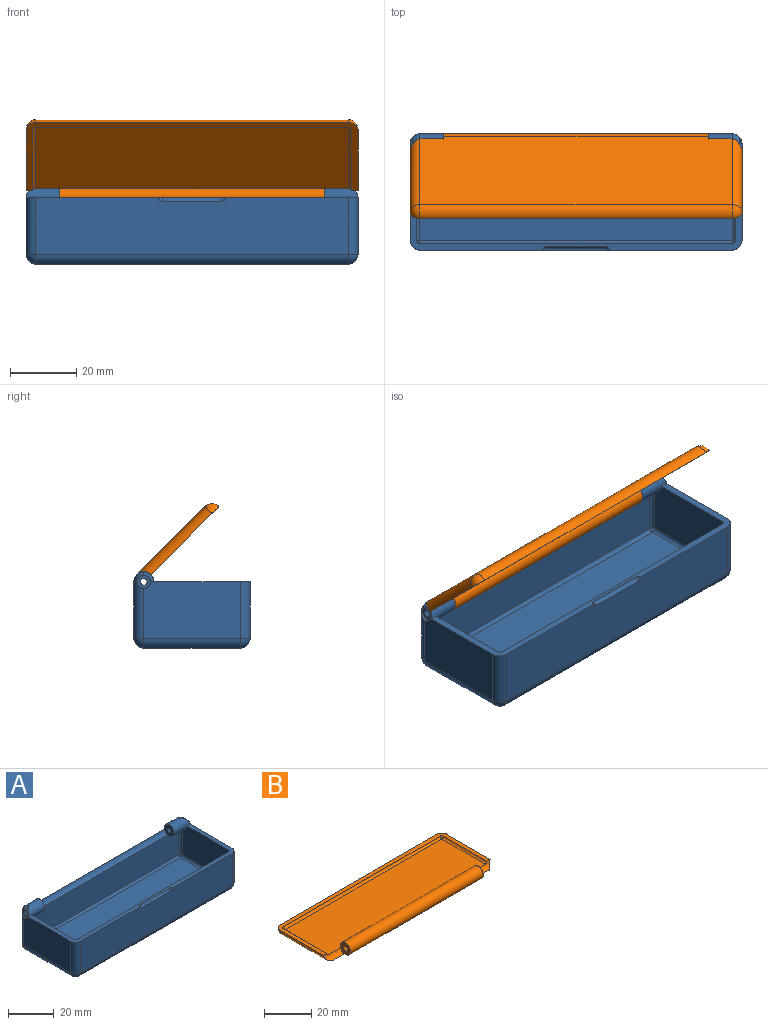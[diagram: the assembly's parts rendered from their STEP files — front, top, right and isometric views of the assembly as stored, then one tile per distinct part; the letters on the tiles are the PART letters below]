
ASSEMBLY  parts=2 mates=1
PART A: 53 faces, bbox 100x35x23 mm
  f0: plane 94x17mm, normal (0,-1,0), area 1578.4mm2, adj f1,f12,f13,f19,f50,f51,f52
  f1: plane 100x29mm, normal (0,0,1), area 285mm2, adj f0,f6,f9,f11,f12,f13,f23,f29
  f2: cylinder r=3mm len=17mm, axis (0,0,-1), area 76.8mm2, adj f5,f9,f10,f16,f24
  f3: cylinder r=3mm len=17mm, axis (0,0,-1), area 76.8mm2, adj f7,f10,f11,f20,f25
  f4: cylinder r=3mm len=3mm, axis (0,-1,0), area 5.6mm2, adj f5,f6,f9,f24
  f5: sphere r=3mm, area 10.5mm2, adj f2,f4,f6,f24
  f6: cylinder r=3mm len=10mm, axis (1,0,0), area 120.6mm2, adj f1,f4,f5,f10,f28,f29,f30,f47
  f7: sphere r=3mm, area 10.5mm2, adj f3,f8,f23,f25
  f8: cylinder r=3mm len=3mm, axis (0,1,0), area 5.6mm2, adj f7,f11,f23,f25
  f9: plane 29x17mm, normal (1,0,0), area 489.9mm2, adj f1,f2,f4,f13,f15,f24
  f10: plane 94x17mm, normal (0,1,0), area 1535.5mm2, adj f2,f3,f6,f18,f23,f45,f46,f47
  f11: plane 29x17mm, normal (-1,0,0), area 489.9mm2, adj f1,f3,f8,f12,f22,f25
  f12: cylinder r=3mm len=17mm, axis (0,0,-1), area 80.1mm2, adj f0,f1,f11,f21
  f13: cylinder r=3mm len=17mm, axis (0,0,-1), area 80.1mm2, adj f0,f1,f9,f17
  f14: plane 94x29mm, normal (0,0,-1), area 2726mm2, adj f15,f18,f19,f22
  f15: cylinder r=3mm len=29mm, axis (0,1,0), area 136.7mm2, adj f9,f14,f16,f17
  f16: sphere r=3mm, area 14.1mm2, adj f2,f15,f18
  f17: sphere r=3mm, area 14.1mm2, adj f13,f15,f19
  f18: cylinder r=3mm len=94mm, axis (-1,0,0), area 443mm2, adj f10,f14,f16,f20
  f19: cylinder r=3mm len=94mm, axis (1,0,0), area 443mm2, adj f0,f14,f17,f21
  f20: sphere r=3mm, area 14.1mm2, adj f3,f18,f22
  f21: sphere r=3mm, area 14.1mm2, adj f12,f19,f22
  f22: cylinder r=3mm len=29mm, axis (0,-1,0), area 136.7mm2, adj f11,f14,f20,f21
  f23: cylinder r=3mm len=10mm, axis (1,0,0), area 120.6mm2, adj f1,f7,f8,f10,f28,f31,f32,f46
  f24: cylinder r=2mm len=4mm, axis (1,0,0), area 7.9mm2, adj f2,f4,f5,f9,f48
  f25: cylinder r=2mm len=4mm, axis (1,0,0), area 7.9mm2, adj f3,f7,f8,f11,f49
  f26: cylinder r=1mm len=9mm, axis (1,0,0), area 56.5mm2, adj f46,f49
  f27: cylinder r=1mm len=9mm, axis (1,0,0), area 56.5mm2, adj f47,f48
  f28: plane 94x14.17mm, normal (0,-1,0), area 1323.7mm2, adj f6,f23,f30,f31,f44,f45,f46,f47
  f29: plane 29x17mm, normal (-1,0,0), area 485.9mm2, adj f1,f6,f30,f35,f41
  f30: cylinder r=1mm len=14.17mm, axis (0,0,-1), area 22.1mm2, adj f6,f28,f29,f43
  f31: cylinder r=1mm len=14.17mm, axis (0,0,-1), area 22.1mm2, adj f23,f28,f32,f42
  f32: plane 29x17mm, normal (1,0,0), area 485.9mm2, adj f1,f23,f31,f33,f40
  f33: cylinder r=1mm len=17mm, axis (0,0,-1), area 26.7mm2, adj f1,f32,f34,f38
  f34: plane 94x17mm, normal (0,1,0), area 1598mm2, adj f1,f33,f35,f37
  f35: cylinder r=1mm len=17mm, axis (0,0,-1), area 26.7mm2, adj f1,f29,f34,f39
  f36: plane 94x29mm, normal (0,0,1), area 2726mm2, adj f37,f40,f41,f44
  f37: cylinder r=1mm len=94mm, axis (1,0,0), area 147.7mm2, adj f34,f36,f38,f39
  f38: sphere r=1mm, area 1.6mm2, adj f33,f37,f40
  f39: sphere r=1mm, area 1.6mm2, adj f35,f37,f41
  f40: cylinder r=1mm len=29mm, axis (0,-1,0), area 45.6mm2, adj f32,f36,f38,f42
  f41: cylinder r=1mm len=29mm, axis (0,1,0), area 45.6mm2, adj f29,f36,f39,f43
  f42: sphere r=1mm, area 1.6mm2, adj f31,f40,f44
  f43: sphere r=1mm, area 1.6mm2, adj f30,f41,f44
  f44: cylinder r=1mm len=94mm, axis (-1,0,0), area 147.7mm2, adj f28,f36,f42,f43
  f45: cylinder r=3.1mm len=80mm, axis (1,0,0), area 244.9mm2, adj f10,f28,f46,f47
  f46: plane 6x6mm, normal (1,0,0), area 25.5mm2, adj f10,f23,f26,f28,f45
  f47: plane 6x6mm, normal (-1,0,0), area 25.5mm2, adj f6,f10,f27,f28,f45
  f48: plane 4x4mm, normal (1,0,0), area 9.4mm2, adj f24,f27
  f49: plane 4x4mm, normal (-1,0,0), area 9.4mm2, adj f25,f26
  f50: cylinder r=1mm len=18mm, axis (1,0,0), area 28.3mm2, adj f0,f1,f51,f52
  f51: sphere r=1mm, area 1.6mm2, adj f0,f1,f50
  f52: sphere r=1mm, area 1.6mm2, adj f0,f1,f50
PART B: 19 faces, bbox 100x35x6 mm
  f0: plane 100x28.9mm, normal (0,0,1), area 304.2mm2, adj f3,f4,f5,f6,f7,f9,f10,f11
  f1: cylinder r=3mm len=79.6mm, axis (1,0,0), area 1206.5mm2, adj f2,f8,f14,f16
  f2: plane 94x29mm, normal (0,0,-1), area 2714.8mm2, adj f1,f3,f4,f7,f14,f15,f16,f17
  f3: cylinder r=3mm len=28.22mm, axis (0,-1,0), area 126.7mm2, adj f0,f2,f5,f17
  f4: cylinder r=3mm len=28.22mm, axis (0,1,0), area 126.7mm2, adj f0,f2,f6,f15
  f5: sphere r=3mm, area 14.1mm2, adj f0,f3,f7
  f6: sphere r=3mm, area 14.1mm2, adj f0,f4,f7
  f7: cylinder r=3mm len=94mm, axis (-1,0,0), area 443mm2, adj f0,f2,f5,f6
  f8: plane 94x26.17mm, normal (0,0,1), area 2458.6mm2, adj f1,f9,f10,f13,f14,f15,f16,f17
  f9: cylinder r=1mm len=26.07mm, axis (0,-1,0), area 40.8mm2, adj f0,f8,f11,f17
  f10: cylinder r=1mm len=26.07mm, axis (0,1,0), area 40.8mm2, adj f0,f8,f12,f15
  f11: sphere r=1mm, area 1.6mm2, adj f0,f9,f13
  f12: sphere r=1mm, area 1.6mm2, adj f0,f10,f13
  f13: cylinder r=1mm len=94mm, axis (-1,0,0), area 147.7mm2, adj f0,f8,f11,f12
  f14: plane 6x6mm, normal (1,0,0), area 24.1mm2, adj f1,f2,f8,f15,f18
  f15: cylinder r=3.1mm len=10.2mm, axis (1,0,0), area 29.9mm2, adj f0,f2,f4,f8,f10,f14
  f16: plane 6x6mm, normal (-1,0,0), area 24.1mm2, adj f1,f2,f8,f17,f18
  f17: cylinder r=3.1mm len=10.2mm, axis (1,0,0), area 29.9mm2, adj f0,f2,f3,f8,f9,f16
  f18: cylinder r=1.2mm len=79.6mm, axis (1,0,0), area 600.2mm2, adj f14,f16
PLACE A t=(0,-202.59,-18.59)mm
PLACE B rot(axis=(1,0,0),135deg) t=(0,-180.89,26.08)mm
MATE revolute B.f1 <-> A.f6  axis (1,0,0) through (39.8,-160.47,1.41)mm
